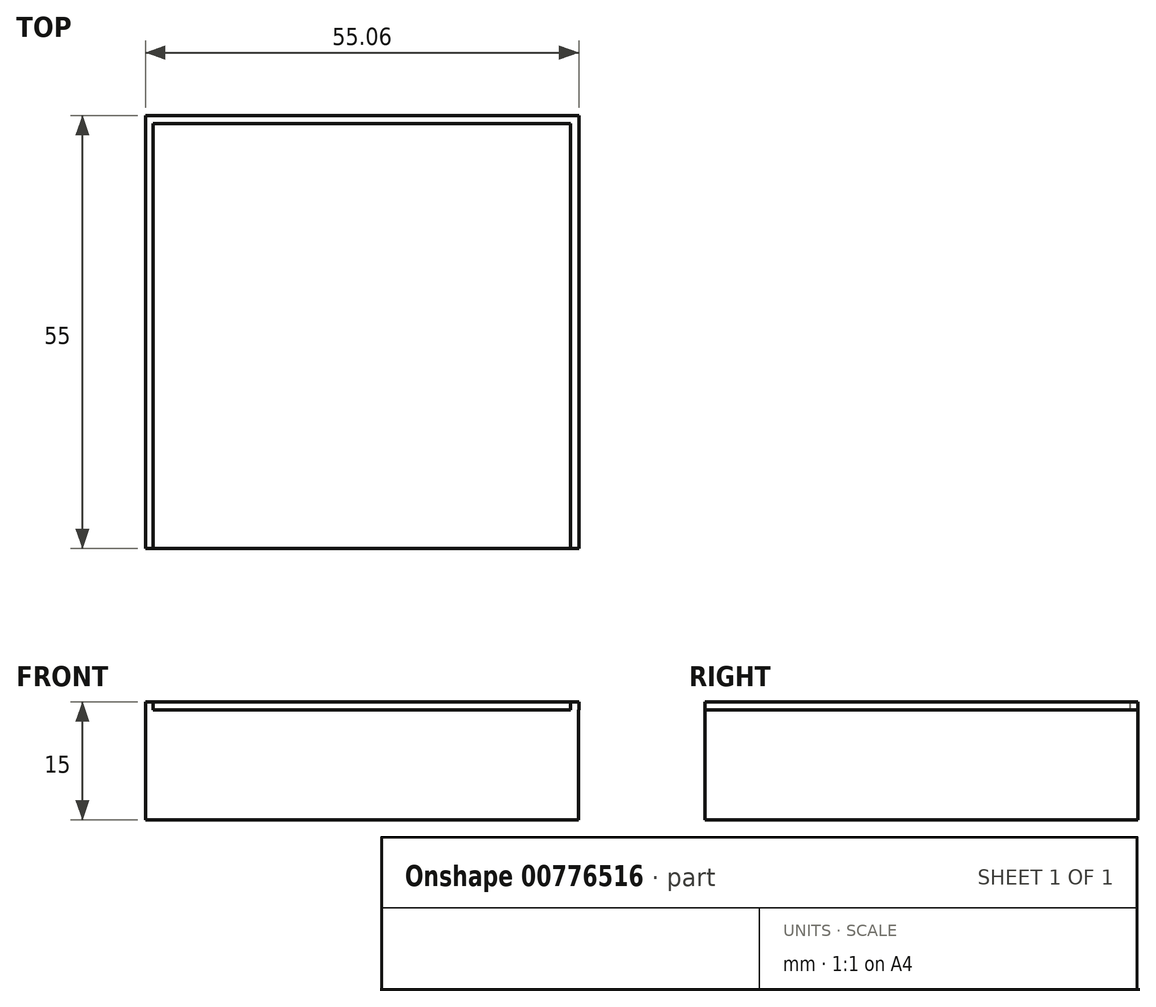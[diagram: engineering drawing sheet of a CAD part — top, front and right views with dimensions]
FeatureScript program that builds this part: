
annotation { "Feature Type Name" : "Feature", "Feature Type Description" : "" }
export const myFeature = defineFeature(function(context is Context, id is Id, definition is map)
    precondition{}
    {
        {
            var Q0;
            Q0=qCreatedBy(makeId("Top.planeOp"),FACE);
            var sketch = newSketch(context, id + "F0", { "sketchPlane" : qUnion([Q0])});
            skLineSegment(sketch, "E0.bottom", {"start": v(0, 0) * mm, "end": v(55, 0) * mm});
            skLineSegment(sketch, "E0.top", {"start": v(0, -55) * mm, "end": v(55, -55) * mm});
            skLineSegment(sketch, "E0.left", {"start": v(0, 0) * mm, "end": v(0, -55) * mm});
            skLineSegment(sketch, "E0.right", {"start": v(55, 0) * mm, "end": v(55, -55) * mm});
            skSolve(sketch);
        }
        {
            var Q0;
            Q0=makeQuery(id+"F0.imprint","IMPRINT",FACE,{"disambiguationData":[TD([[makeQuery(id+"F0.imprint","IMPRINT",EDGE,{"derivedFrom":sQuery(id+"F0.wireOp",EDGE,"E0.bottom")}),-1.0]])]});
            var sketch = newSketch(context, id + "F1", { "sketchPlane" : qUnion([Q0])});
            skLineSegment(sketch, "E1.0", {"start": v(54, -1) * mm, "end": v(54, -55) * mm});
            skLineSegment(sketch, "E1.1", {"start": v(1, -1) * mm, "end": v(54, -1) * mm});
            skLineSegment(sketch, "E1.2", {"start": v(1, -1) * mm, "end": v(1, -55) * mm});
            skLineSegment(sketch, "E2", {"start": v(1, -55) * mm, "end": v(0, -55) * mm});
            skLineSegment(sketch, "E3", {"start": v(0, -55) * mm, "end": v(0, 0) * mm});
            skLineSegment(sketch, "E4", {"start": v(0, 0) * mm, "end": v(55.06, 0) * mm});
            skLineSegment(sketch, "E5", {"start": v(55.06, 0) * mm, "end": v(55.06, -55) * mm});
            skLineSegment(sketch, "E6", {"start": v(54, -55) * mm, "end": v(55.06, -55) * mm});
            skSolve(sketch);
        }
        {
            var Q0;
            Q0 = qSketchRegion(id + "F1", true);
            extrude(context, id + "F2", {"entities" : qUnion([Q0]), "depth" : 1 * mm, "offsetDistance" : 25 * mm});
        }
        {
            var Q0;
            Q0 = qSketchRegion(id + "F0", true);
            extrude(context, id + "F3", {"entities" : qUnion([Q0]), "operationType" : NewBodyOperationType.ADD, "oppositeDirection" : true, "depth" : 14 * mm, "offsetDistance" : 25 * mm});
        }
    });
